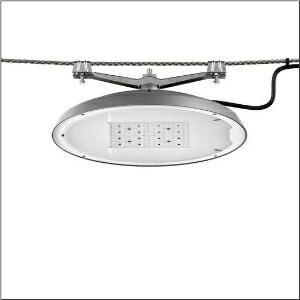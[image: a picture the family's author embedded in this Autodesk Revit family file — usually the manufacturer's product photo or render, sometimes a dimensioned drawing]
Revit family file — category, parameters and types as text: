
# Revit family: dl_r__50_iq_mini___st0_8s_5xa248v31f08le_222e
name_source: partatom
category: Lighting Fixtures
units: mm (PartAtom-declared; Revit-internal decimal feet)

## family parameters
Cut with Voids When Loaded = No
Host = Face
Light Source = No
Part Type = Normal
Room Calculation Point = No
Round Connector Dimension = Use Diameter
Shared = No

## types (1)
- --- (1 x LED, 10390 lm, 67.4 W, 3000K)
    Apparent Load = 67 VA
    CIE Flux Codes = 38 75 97 100 100
    Color Rendering = 70
    Color Temperature = 3000K
    Default Elevation = 1800 mm
    Description = DL® 50 iQ mini, catenary luminaire, primary light control with lens, of PMMA, primary optical cover: cover, of toughened safety glass, transparent, light distribution: ST0.8s, light emission: direct distribution, primary light characteristic: symmetric, installation type: suspended mounting, LED, High Power LED, rated luminous flux: 10.390lm, luminous efficacy: 154lm/W, light colour: 730, colour temperature: 3000K, control gear: iQ Street-Remote, control: optimised constant luminous flux control (CLO 2.0), Desk-Remote (wireless, voltage-free reading and setting of iQ features in the workshop via application-optimized NFC function/RFID function), Light-Fading, Smart-Wire, Night-Set, Lumen-Switch, Temp-Guard, Auto-Match, Street-Remote, mains connection: 230..240V, AC, 50/60Hz, start of lifetime: 67W, end of service life: 70W, reduction: 31W, luminaire housing, of diecast aluminium, powder-coated, Siteco® metallic grey (DB 702S), diameter: 500mm, height: 115mm, mounting height: 4..12m, protection rating (complete): IP66, insulation class (complete): insulation class II (safety insulation), certification: CE, ENEC, ENEC+, VDE, impact resistance: IK08, permissible operating ambient temperature for outdoor applications: -25..+40°C, standard-compliant lighting for roads and squares, packaging unit: 1 piece

Light Distribution: ST0.8s
    Height = 124 mm  [stored 0.406824 ft]
    Lamp = 1 x LED
    Lamp Light Flux = 10390 lm
    Lamp Power = 67.4 W
    Lamp count = 1
    Length = 500 mm
    Luminous efficacy = 154 lm/W
    Manufacturer = Siteco
    ModVariant = No
    Model = 5XA248V31F08LE
    Number of Poles = 1
    OnlyDefault = Yes
    Power Factor = 1
    Product Name = DL® 50 iQ mini | ST0.8s
    Product group = catenary luminaire
    ProductGroupID = 6300
    Protection Class = Protection class II
    Protection Degree = IP 66
    RLX_Detail_Level = 1
    RLX_Emergency_Light_Flux = 0 lm
    RLX_Emergency_Type = 0
    RLX_Emergency_Type_DB = No
    RlxData = <blob elided: 127209 chars, md5=65700033>
    Socket = socket
    Standby Power = 0 W
    System Light Flux = 10390 lm
    System Power = 67 W
    Type Comments = factory setting: luminous flux: 100 % | dim-lin: 254 | 705 mA
    Type Image = l_1251783.jpg
    URL = http://relux.com
    VarID = @adj_162537
    Voltage = 0 V
    Weight = 0.00 kg
    Width = 0 mm  [stored 0 ft]

note: [stored X ft] marks values corroborated as IEEE doubles in the binary element streams (Revit-internal decimal feet)

## geometry (parser evidence)
native form markers: Blend x4, Sweep x14
no freeform markers — native parametric forms only
